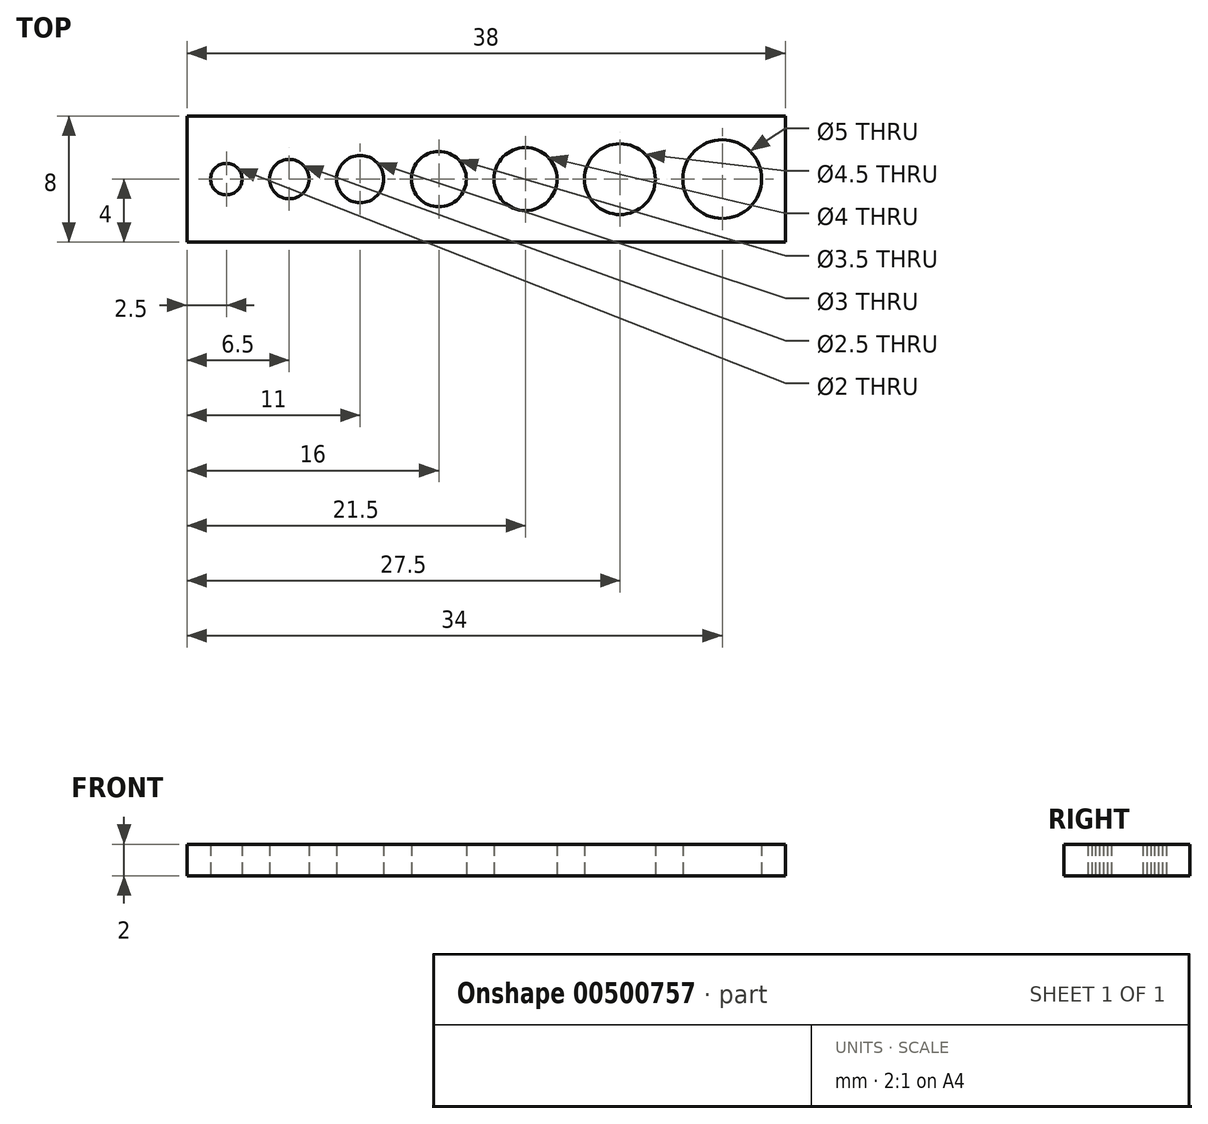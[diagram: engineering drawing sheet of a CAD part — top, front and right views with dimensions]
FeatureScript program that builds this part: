
annotation { "Feature Type Name" : "Feature", "Feature Type Description" : "" }
export const myFeature = defineFeature(function(context is Context, id is Id, definition is map)
    precondition{}
    {
        {
            var Q0;
            Q0=qCreatedBy(makeId("Top.planeOp"),FACE);
            var sketch = newSketch(context, id + "F0", { "sketchPlane" : qUnion([Q0])});
            skLineSegment(sketch, "E0.bottom", {"start": v(-21.5, 4) * mm, "end": v(16.5, 4) * mm});
            skLineSegment(sketch, "E0.top", {"start": v(-21.5, -4) * mm, "end": v(16.5, -4) * mm});
            skLineSegment(sketch, "E0.left", {"start": v(-21.5, 4) * mm, "end": v(-21.5, -4) * mm});
            skLineSegment(sketch, "E0.right", {"start": v(16.5, 4) * mm, "end": v(16.5, -4) * mm});
            skCircle(sketch, "E1", {"center": v(12.5, 0) * mm, "radius": 2.5 * mm});
            skCircle(sketch, "E2", {"center": v(6, 0) * mm, "radius": 2.25 * mm});
            skCircle(sketch, "E3", {"center": v(0, 0) * mm, "radius": 2 * mm});
            skCircle(sketch, "E4", {"center": v(-5.5, 0) * mm, "radius": 1.75 * mm});
            skCircle(sketch, "E5", {"center": v(-10.5, 0) * mm, "radius": 1.5 * mm});
            skCircle(sketch, "E6", {"center": v(-15, 0) * mm, "radius": 1.25 * mm});
            skCircle(sketch, "E7", {"center": v(-19, 0) * mm, "radius": 1 * mm});
            skSolve(sketch);
        }
        {
            var Q0;
            Q0=makeQuery(id+"F0.imprint","IMPRINT",FACE,{"disambiguationData":[TD([[makeQuery(id+"F0.imprint","IMPRINT",EDGE,{"derivedFrom":sQuery(id+"F0.wireOp",EDGE,"E0.bottom")}),-1.0]])]});
            extrude(context, id + "F1", {"entities" : qUnion([Q0]), "depth" : 2 * mm, "offsetDistance" : 25 * mm});
        }
    });
